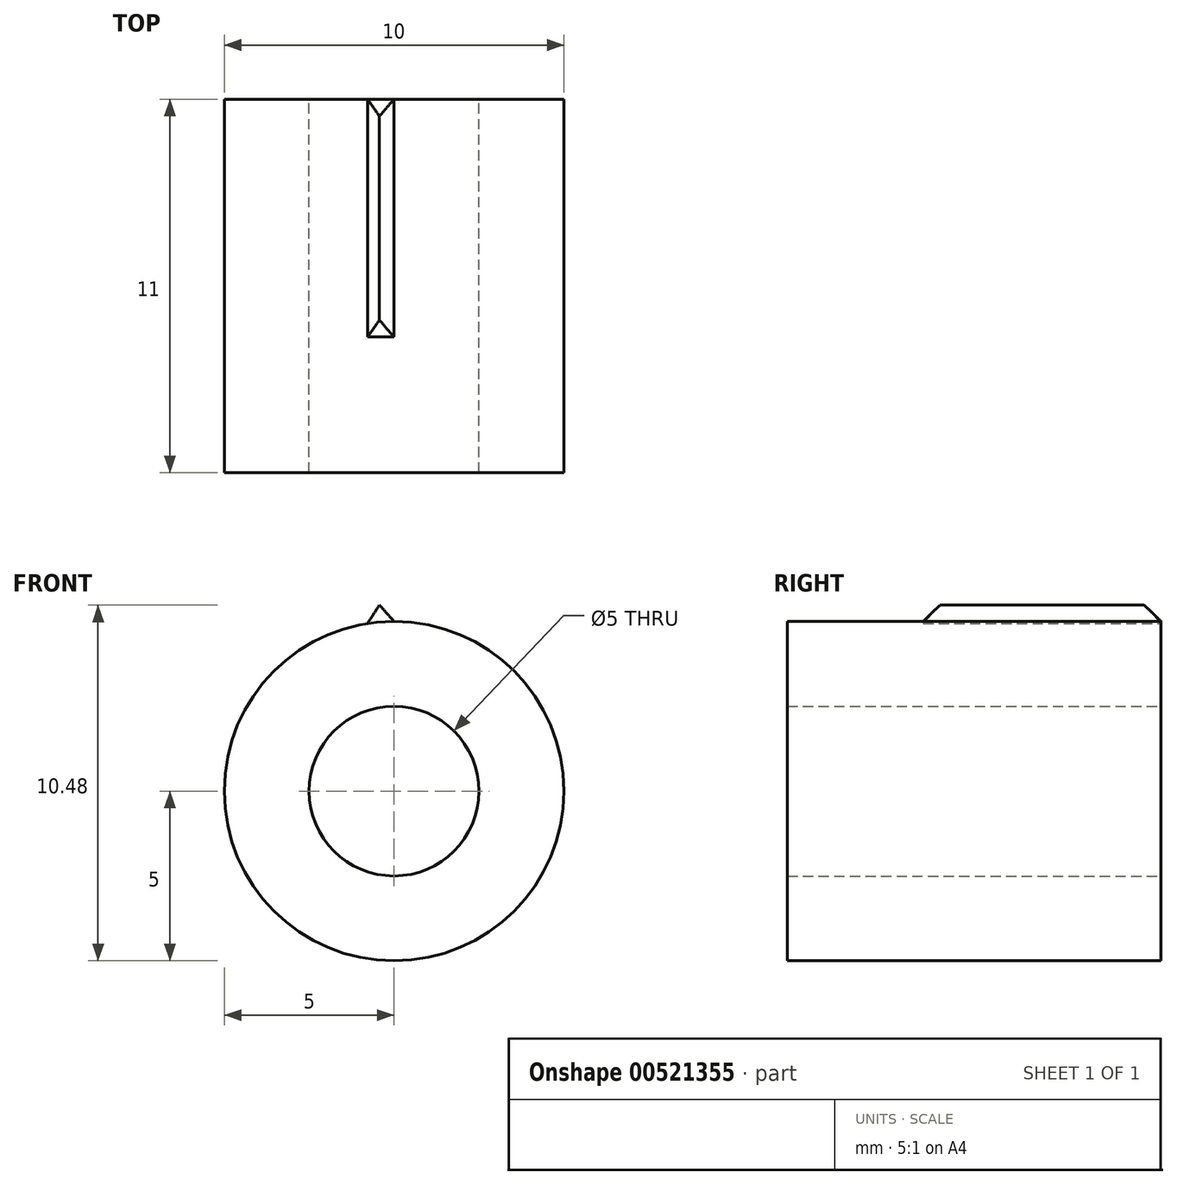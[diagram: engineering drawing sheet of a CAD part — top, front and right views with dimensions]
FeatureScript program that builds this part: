
annotation { "Feature Type Name" : "Feature", "Feature Type Description" : "" }
export const myFeature = defineFeature(function(context is Context, id is Id, definition is map)
    precondition{}
    {
        {
            var Q0;
            Q0=qCreatedBy(makeId("Front.planeOp"),FACE);
            var sketch = newSketch(context, id + "F0", { "sketchPlane" : qUnion([Q0])});
            skCircle(sketch, "E0", {"center": v(0, 0) * mm, "radius": 5.5 * mm, "construction": true});
            skCircle(sketch, "E1", {"center": v(0, 0) * mm, "radius": 5 * mm});
            skLineSegment(sketch, "E2", {"start": v(0, 0) * mm, "end": v(0, 5.5) * mm, "construction": true});
            skLineSegment(sketch, "E3", {"start": v(0, 0) * mm, "end": v(-0.86, 5.43) * mm, "construction": true});
            skLineSegment(sketch, "E4", {"start": v(0, 0) * mm, "end": v(-0.43, 5.48) * mm, "construction": true});
            skLineSegment(sketch, "E5", {"start": v(0, 5) * mm, "end": v(-0.43, 5.48) * mm});
            skLineSegment(sketch, "E6", {"start": v(-0.43, 5.48) * mm, "end": v(-0.78, 4.94) * mm});
            skCircle(sketch, "E7", {"center": v(0, 0) * mm, "radius": 2.5 * mm});
            skSolve(sketch);
        }
        {
            var Q0;
            {var subQ0=sQuery(id+"F0.wireOp",EDGE,"E1");var subQ1=makeQuery(id+"F0.imprint","INTERSECT",VERTEX,{"derivedFrom":[subQ0,sQuery(id+"F0.wireOp",EDGE,"E5")]});Q0=makeQuery(id+"F0.imprint","IMPRINT",FACE,{"disambiguationData":[TD([[makeQuery(id+"F0.imprint","IMPRINT",EDGE,{"disambiguationData":[TD([[subQ1,-1.0]])],"derivedFrom":subQ0}),1.0]])]});}
            extrude(context, id + "F1", {"entities" : qUnion([Q0]), "depth" : 11 * mm, "offsetDistance" : 25 * mm});
        }
        {
            var Q0;
            {var subQ0=sQuery(id+"F0.wireOp",EDGE,"E5");Q0=makeQuery(id+"F0.imprint","IMPRINT",FACE,{"disambiguationData":[TD([[makeQuery(id+"F0.imprint","IMPRINT",EDGE,{"derivedFrom":subQ0}),1.0]])]});}
            extrude(context, id + "F2", {"entities" : qUnion([Q0]), "operationType" : NewBodyOperationType.ADD, "depth" : 7 * mm, "offsetDistance" : 25 * mm});
        }
        {
            var Q0;
            Q0=qCreatedBy(makeId("Top.planeOp"),FACE);
            var sketch = newSketch(context, id + "F3", { "sketchPlane" : qUnion([Q0])});
            skLineSegment(sketch, "E8", {"start": v(0, 0) * mm, "end": v(0, -15.45) * mm, "construction": true});
            skLineSegment(sketch, "E9", {"start": v(5, 0) * mm, "end": v(7, -2) * mm});
            skLineSegment(sketch, "E10", {"start": v(7, -2) * mm, "end": v(7, -5) * mm});
            skLineSegment(sketch, "E11", {"start": v(7, -5) * mm, "end": v(5, -7) * mm});
            skLineSegment(sketch, "E12.0", {"start": v(5, 0) * mm, "end": v(-5, 0) * mm, "construction": true});
            skLineSegment(sketch, "E13", {"start": v(5, 0) * mm, "end": v(8, 0) * mm});
            skLineSegment(sketch, "E14", {"start": v(8, 0) * mm, "end": v(8, -7) * mm});
            skLineSegment(sketch, "E15", {"start": v(8, -7) * mm, "end": v(5, -7) * mm});
            skSolve(sketch);
        }
        {
            var Q0;
            Q0 = qSketchRegion(id + "F3", true);
            var Q1;
            Q1=sQuery(id+"F3.wireOp",EDGE,"E8");
            revolve(context, id + "F4", {"operationType" : NewBodyOperationType.REMOVE, "entities" : qUnion([Q0]), "axis" : qUnion([Q1]), "revolveType" : RevolveType.FULL, "oppositeDirection" : true});
        }
    });
